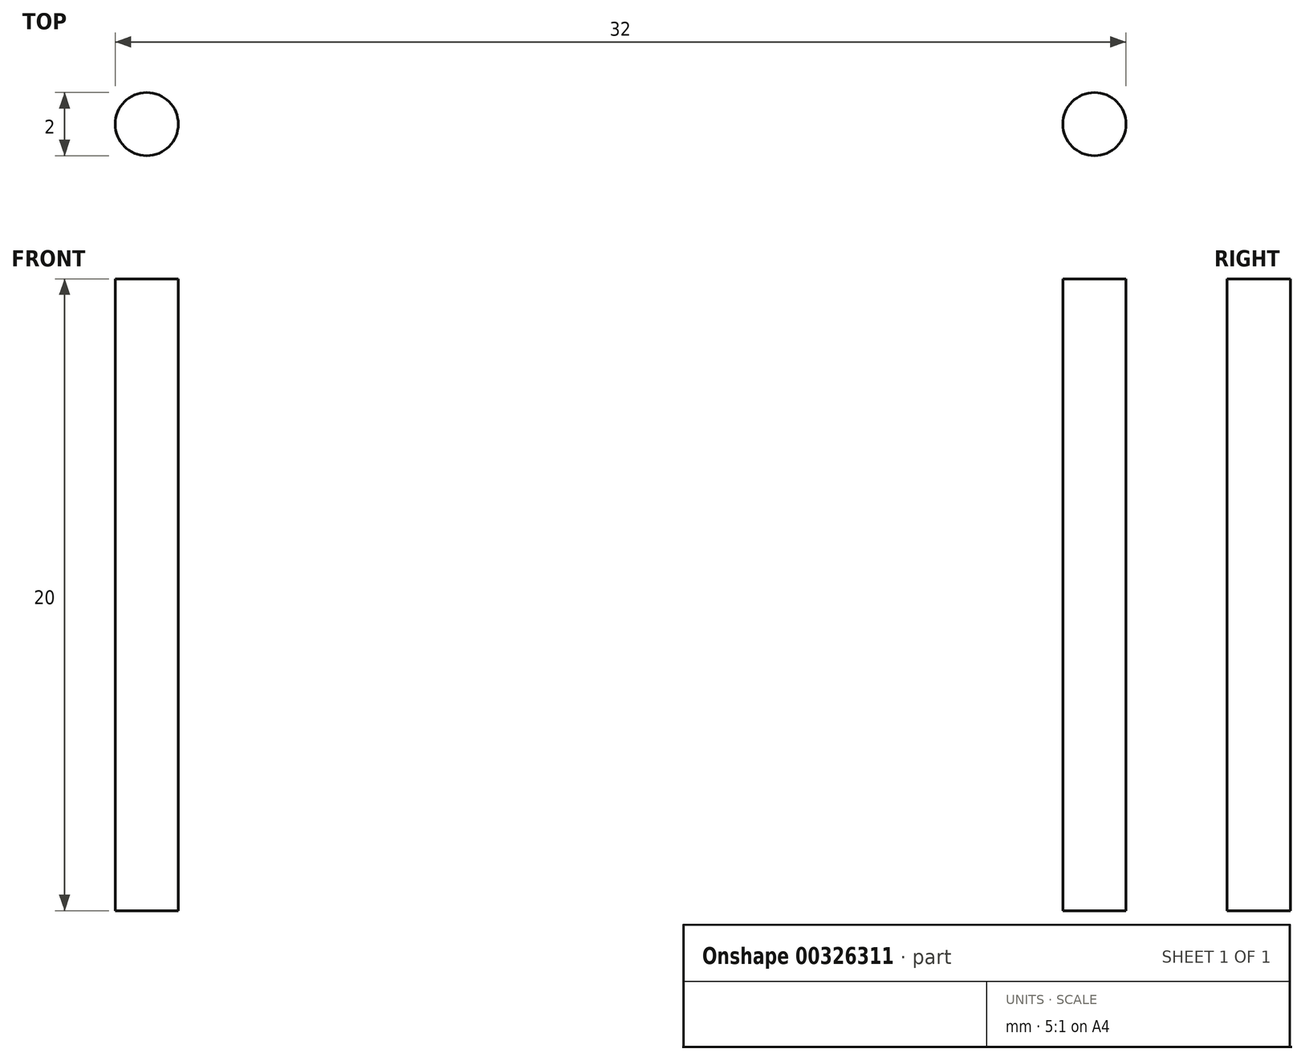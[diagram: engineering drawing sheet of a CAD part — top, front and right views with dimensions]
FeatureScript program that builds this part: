
annotation { "Feature Type Name" : "Feature", "Feature Type Description" : "" }
export const myFeature = defineFeature(function(context is Context, id is Id, definition is map)
    precondition{}
    {
        {
            var Q0;
            Q0=qCreatedBy(makeId("Top.planeOp"),FACE);
            var sketch = newSketch(context, id + "F0", { "sketchPlane" : qUnion([Q0])});
            skCircle(sketch, "E0", {"center": v(-15, 0) * mm, "radius": 1 * mm});
            skCircle(sketch, "E1.MirrorC", {"center": v(15, 0) * mm, "radius": 1 * mm});
            skSolve(sketch);
        }
        {
            var Q0;
            Q0 = qSketchRegion(id + "F0", true);
            extrude(context, id + "F1", {"entities" : qUnion([Q0]), "depth" : 20 * mm, "offsetDistance" : 25 * mm});
        }
    });
